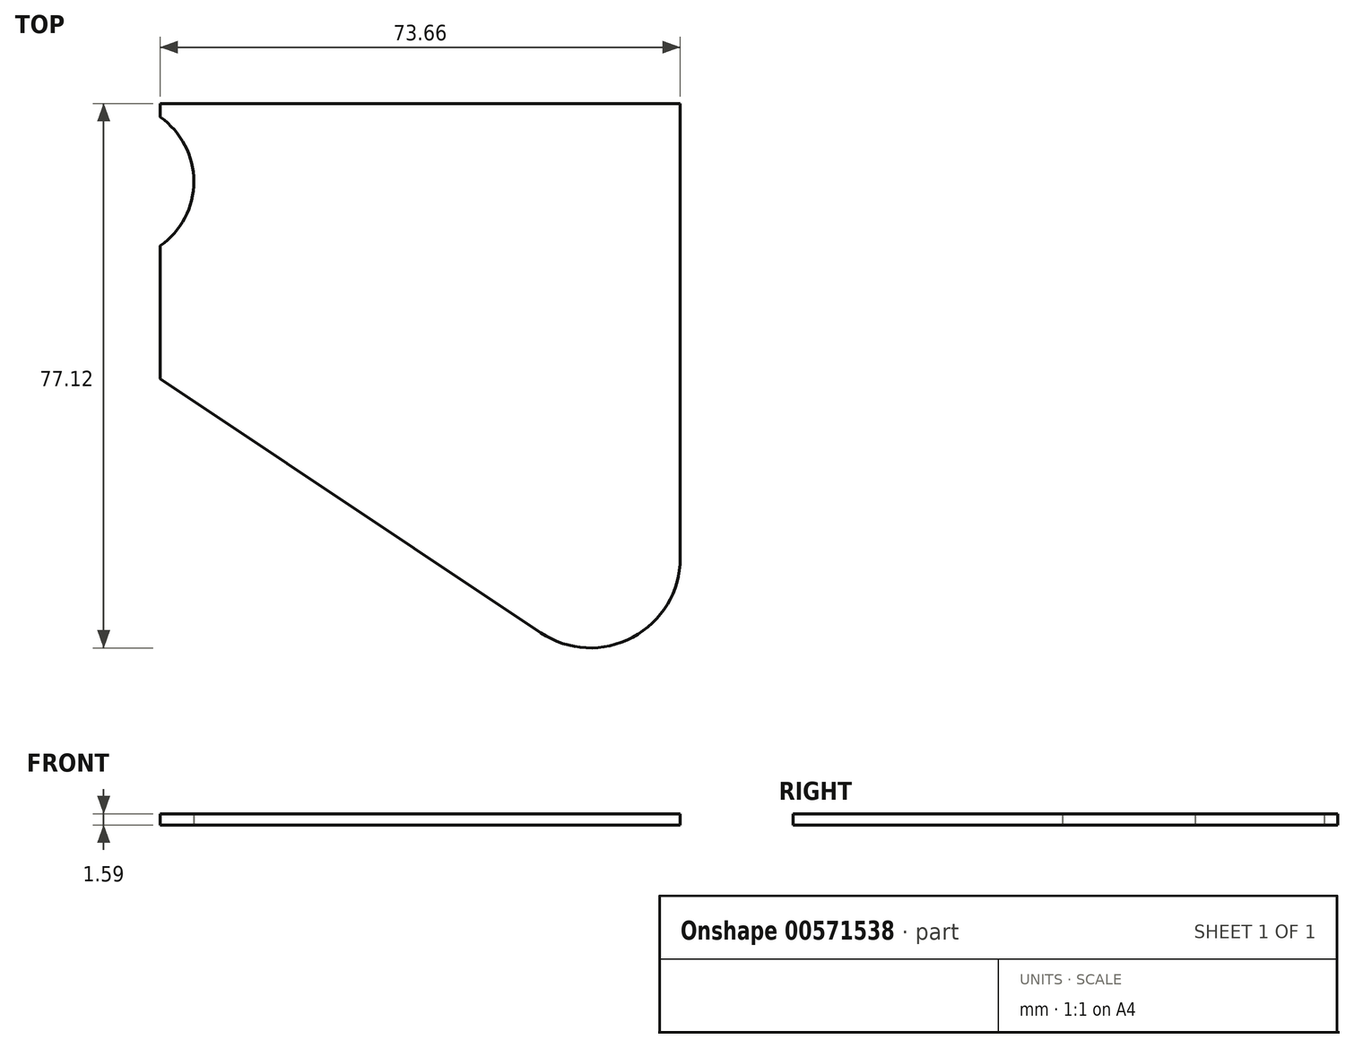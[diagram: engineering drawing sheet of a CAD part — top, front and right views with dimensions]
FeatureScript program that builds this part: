
annotation { "Feature Type Name" : "Feature", "Feature Type Description" : "" }
export const myFeature = defineFeature(function(context is Context, id is Id, definition is map)
    precondition{}
    {
        {
            var Q0;
            Q0=qCreatedBy(makeId("Top.planeOp"),FACE);
            var sketch = newSketch(context, id + "F0", { "sketchPlane" : qUnion([Q0])});
            skCircle(sketch, "E0", {"center": v(0, 0) * mm, "radius": 11.11 * mm, "construction": true});
            skCircle(sketch, "E1", {"center": v(0, 0) * mm, "radius": 6.35 * mm, "construction": true});
            skLineSegment(sketch, "E2", {"start": v(6.35, 0) * mm, "end": v(6.35, 9.12) * mm, "construction": true});
            skLineSegment(sketch, "E3", {"start": v(6.35, 9.12) * mm, "end": v(6.35, 11.02) * mm});
            skLineSegment(sketch, "E4", {"start": v(6.35, 11.02) * mm, "end": v(80, 11.02) * mm});
            skLineSegment(sketch, "E5", {"start": v(80, 11.02) * mm, "end": v(80, -53.4) * mm});
            skLineSegment(sketch, "E6", {"start": v(80, -55.02) * mm, "end": v(80, -66.2) * mm});
            skLineSegment(sketch, "E7", {"start": v(80, -66.2) * mm, "end": v(58.42, -66.2) * mm});
            skLineSegment(sketch, "E8", {"start": v(11.11, -31.12) * mm, "end": v(60.25, -63.96) * mm});
            skPoint(sketch, "E9.newPointB", {"position": v(80, -55.02) * mm});
            skArc(sketch, "E9.filletArc", {"start": v(60.25, -63.96) * mm, "mid": v(73.3, -64.6) * mm, "end": v(80.01, -53.4) * mm});
            skLineSegment(sketch, "E10", {"start": v(6.35, 0) * mm, "end": v(6.35, -9.12) * mm, "construction": true});
            skLineSegment(sketch, "E11", {"start": v(11.11, -31.12) * mm, "end": v(6.35, -27.93) * mm});
            skLineSegment(sketch, "E12", {"start": v(6.35, -9.12) * mm, "end": v(6.35, -27.93) * mm});
            skArc(sketch, "E13", {"start": v(6.35, -9.12) * mm, "mid": v(11.11, 0) * mm, "end": v(6.35, 9.12) * mm});
            skSolve(sketch);
        }
        {
            var Q0;
            Q0=qSketchRegion(id+"F0",true);
            extrude(context, id + "F1", {"entities" : qUnion([Q0]), "depth" : 1.59 * mm});
        }
    });
